# Revit family: Hager-WITTY EVOLUTIVE-fr-FR-FR
name_source: partatom
category: Electrical Fixtures
units: mm (PartAtom-declared; Revit-internal decimal feet)

## family parameters
Always vertical = Yes
Cut with Voids When Loaded = No
Host = Wall
Maintain Annotation Orientation = No
OmniClass Number = 23.80.00.00
OmniClass Title = Electric Power and Lighting
Part Type = Normal
Room Calculation Point = No
Round Connector Dimension = Use Diameter
Shared = No

## types (12) — shared parameters
Arrondi = 30 mm  [stored 0.0984252 ft]
BC_MODEL_ID = 1043718
BC_OBJECT_ID = 349814
BC_OBJECT_VERSION = #1
Code hager = ADD-EC002883_EVCS
Default Elevation = 1000 mm  [stored 3.28084 ft]
HG000003-Gamme = WITTY EVOLUTIVE
HG000059-Operating voltage = 410 V
HG000099-Onfly Template ID = 1043713
Manufacturer = hager
Name = Template-EVCS-ParkEvolutive_EU-EC002883
Name BIM&CO = Workstation equipment
Name hager = ADD_ChargingStation_EC002883
avec affichage = No
avec compteur d'énergie = No
avec gestion de la charge = Yes
compatible IFTTT = No
compatible avec Amazon Alexa = No
compatible avec Apple HomeKit = No
compatible avec Google Assistant = No
hauteur = 549 mm  [stored 1.80118 ft]
indice de protection (IP) = IP55
indice de protection contre les chocs (IK) = IK10
matériau du boîtier/corps = plastique
mode de pose = montage mural
nombre de points de chargement = 1
profondeur = 173 mm
zero-valued in all types: longueur du câble de charge, nombre d'interrupteurs différentiels type B, nombre de coupleurs de charge CHAdeMO, nombre de coupleurs de charge GB CA, nombre de coupleurs de charge GB CC, nombre de coupleurs de charge type 1, nombre de coupleurs de charge type 1 CCS, nombre de coupleurs de charge type 2, nombre de coupleurs de charge type 2 CCS, nombre de prises de charge GB, nombre de prises de courant domestiques

## per-type parameters (varying)
| type | BC_VARIANT_ID | HG000004-Référence fabricant | HG000065-Avec prise TE | Reference description | avec boîte de raccordement domestique | avec disjoncteur de protection | avec interface de communication | exécution raccord côté installation | fonction contrôle d'accès | largeur | nombre d'interrupteurs différentiels type A | nombre de prises CEE | nombre de prises de charge type 2 | nombre de prises de charge type 3 | puissance de raccordement nominale | puissance max. par point de chargement |
| WITTY EVOLUTIVE-1x7KW-1P-XEV1K07T2TETPFR | 842255 | XEV1K07T2TETPFR | Yes | EVSE witty 1x7kW T2+TE+TIC+PFR | No | Yes | No | monophasé | No | 251 mm | 1 | 1 | 1 | 0 | 4000 W | 7000 W |
| WITTY EVOLUTIVE-1x22KW-3P-XEV1K22T2S | 842259 | XEV1K22T2S | No | EVSE witty solar 1x22kW 3P T2 + RFID | No | No | Yes | triphasé | Yes | 251 mm | 0 | 0 | 1 | 0 | 0 W | 22000 W |
| WITTY EVOLUTIVE-1x22KW-3P-XEV1K22T2 | 842258 | XEV1K22T2 | No | EVSE witty 1x22kW 3P T2 with key | No | No | No | triphasé | No | 251 mm | 0 | 0 | 1 | 0 | 11000 W | 22000 W |
| WITTY EVOLUTIVE-1x7KW-1P-XEV1K07T2TPFR | 842257 | XEV1K07T2TPFR | No | EVSE witty 1x7kW T2+TIC+PFR | No | Yes | No | monophasé | No | 251 mm | 1 | 0 | 1 | 0 | 4000 W | 7000 W |
| WITTY EVOLUTIVE-1x22KW-3P-XEV1R22T2 | 842265 | XEV1R22T2 | No | EVSE witty 1x22kW 3P T2 RFID | Yes | No | No | triphasé | Yes | 237 mm  [stored 0.777559 ft] | 0 | 0 | 1 | 0 | 11000 W | 22000 W |
| WITTY EVOLUTIVE-1x22KW-3P-XEV1K22T2TE | 842264 | XEV1K22T2TE | Yes | EVSE witty 1x22kW 3P T2 +TE with key | No | No | No | triphasé | No | 251 mm | 0 | 1 | 1 | 0 | 11000 W | 22000 W |
| WITTY EVOLUTIVE-1x7KW-1P-XEV1K07T2 | 842250 | XEV1K07T2 | No | EVSE witty 1x7kW 1PT2 with key | No | No | No | monophasé | No | 251 mm | 0 | 0 | 0 | 0 | 4000 W | 7000 W |
| WITTY EVOLUTIVE-1x7KW-1P-XEV1K07T2SEMC | 842253 | XEV1K07T2SEMC | No | KIT witty solar 7kW RFID + EMC + PV1P | No | No | Yes | triphasé | Yes | 251 mm | 0 | 0 | 1 | 0 | 0 W | 7000 W |
| WITTY EVOLUTIVE-1x22KW-3P-XEV1R22T2TE | 842266 | XEV1R22T2TE | Yes | EVSE witty 1x22kW 3P T2 +TE RFID | Yes | No | No | triphasé | Yes | 237 mm  [stored 0.777559 ft] | 0 | 1 | 1 | 0 | 11000 W | 22000 W |
| WITTY EVOLUTIVE-1x22KW-3P-XEV1K22T2T | 842262 | XEV1K22T2T | Yes | EVSE witty 1x22kW 3P T2 + TIC with key | No | Yes | Yes | triphasé | No | 251 mm | 0 | 1 | 1 | 1 | 22000 W | 22000 W |
| WITTY EVOLUTIVE-1x22KW-3P-XEV1K22T2SEMC | 842260 | XEV1K22T2SEMC | No | KIT witty solar 22kW/RFID + EMC +PV3P | No | No | Yes | triphasé | Yes | 251 mm | 0 | 0 | 1 | 0 | 0 W | 22000 W |
| WITTY EVOLUTIVE-1x7KW-1P-XEV1K07T2S | 842251 | XEV1K07T2S | No | EVSE witty solar 1x7kW 1P T2 + RFID | No | No | Yes | triphasé | Yes | 251 mm | 0 | 0 | 1 | 0 | 0 W | 7000 W |

note: column(s) folded — value = type name in every type: Reference

note: [stored X ft] marks values corroborated as IEEE doubles in the binary element streams (Revit-internal decimal feet)

## geometry (parser evidence)
native form markers: Sweep x5
no freeform markers — native parametric forms only
